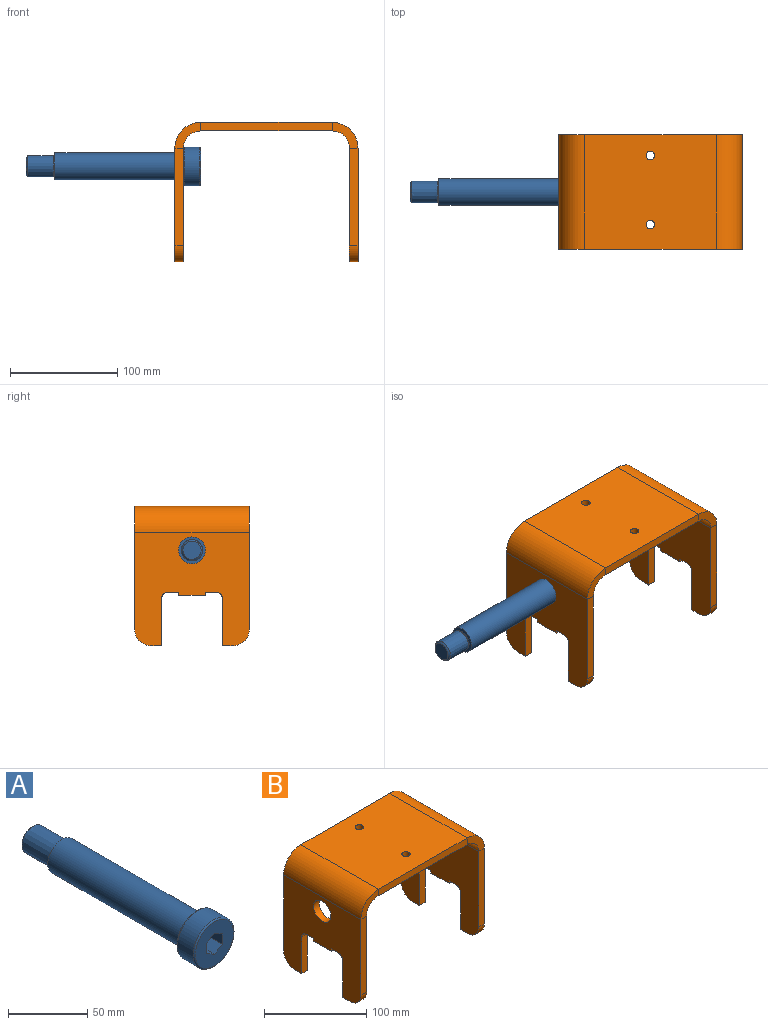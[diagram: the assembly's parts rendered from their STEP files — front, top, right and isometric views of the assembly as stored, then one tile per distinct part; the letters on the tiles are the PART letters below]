
ASSEMBLY  parts=2 mates=1
PART A: 20 faces, bbox 39x163x39 mm
  f0: plane 25x25mm, normal (0,1,0), area 222.1mm2, adj f14,f16
  f1: cylinder r=18mm len=36mm, axis (0,-1,0), area 1583.4mm2, adj f11,f12
  f2: plane 34x34mm, normal (0,1,0), area 492.4mm2, adj f12,f13
  f3: plane 34x34mm, normal (0,-1,0), area 738.2mm2, adj f4,f5,f6,f7,f8,f9,f11
  f4: plane 11x8.08mm, normal (-1,0,0), area 88.9mm2, adj f3,f5,f9,f10
  f5: plane 11x7.01mm, normal (-0.5,0,-0.87), area 88.9mm2, adj f3,f4,f6,f10
  f6: plane 11x6.99mm, normal (0.5,0,-0.86), area 88.9mm2, adj f3,f5,f7,f10
  f7: plane 11x8.08mm, normal (1,0,0), area 88.9mm2, adj f3,f6,f8,f10
  f8: plane 11x7.01mm, normal (0.5,0,0.87), area 88.9mm2, adj f3,f7,f9,f10
  f9: plane 11x6.99mm, normal (-0.5,0,0.86), area 88.9mm2, adj f3,f4,f8,f10
  f10: plane 16.17x14.02mm, normal (0,-1,0), area 169.7mm2, adj f4,f5,f6,f7,f8,f9
  f11: torus R=17mm, axis (0,-1,0), area 174.1mm2, adj f1,f3
  f12: torus R=17mm, axis (0,-1,0), area 174.1mm2, adj f1,f2
  f13: cylinder r=11.5mm len=23mm, axis (0,-1,0), area 108.4mm2, adj f2,f15
  f14: cylinder r=12.5mm len=118.5mm, axis (0,-1,0), area 9307mm2, adj f0,f15
  f15: plane 25x25mm, normal (0,-1,0), area 75.4mm2, adj f13,f14
  f16: bspline ~20x20mm, area 103.4mm2, adj f0,f17
  f17: extruded ~24x20mm, area 1508mm2, adj f16,f19
  f18: plane 17.03x17.02mm, normal (0,1,0), area 227mm2, adj f19
  f19: bspline ~20x20mm, area 123.3mm2, adj f17,f18
PART B: 50 faces, bbox 171x107x130 mm
  f0: plane 123x8mm, normal (0,1,0), area 984mm2, adj f4,f5,f25,f46
  f1: plane 123x8mm, normal (0,-1,0), area 984mm2, adj f4,f5,f24,f47
  f2: cylinder r=4mm len=8mm, axis (0,0,1), area 201.1mm2, adj f4,f5
  f3: cylinder r=4mm len=8mm, axis (0,0,1), area 201.1mm2, adj f4,f5
  f4: plane 123x107mm, normal (0,0,-1), area 13060.5mm2, adj f0,f1,f2,f3,f27,f49
  f5: plane 123x107mm, normal (0,0,1), area 13060.5mm2, adj f0,f1,f2,f3,f26,f48
  f6: plane 9.9x8mm, normal (0,0,-1), area 79.2mm2, adj f7,f18,f19,f20
  f7: plane 8x3mm, normal (0,-1,0), area 24mm2, adj f6,f8,f18,f19
  f8: plane 25x8mm, normal (0,0,-1), area 200mm2, adj f7,f9,f18,f19
  f9: plane 8x3mm, normal (0,1,0), area 24mm2, adj f8,f10,f18,f19
  f10: plane 9.9x8mm, normal (0,0,-1), area 79.2mm2, adj f9,f18,f19,f21
  f11: plane 44x8mm, normal (0,-1,0), area 352mm2, adj f12,f18,f19,f21
  f12: plane 10.1x8mm, normal (0,0,-1), area 80.8mm2, adj f11,f18,f19,f22
  f13: plane 91x8mm, normal (0,1,0), area 728mm2, adj f18,f19,f22,f25
  f14: plane 91x8mm, normal (0,-1,0), area 728mm2, adj f18,f19,f23,f24
  f15: plane 10.1x8mm, normal (0,0,-1), area 80.8mm2, adj f17,f18,f19,f23
  f16: cylinder r=12mm len=24mm, axis (1,0,0), area 603.2mm2, adj f18,f19
  f17: plane 44x8mm, normal (0,1,0), area 352mm2, adj f15,f18,f19,f20
  f18: plane 107x106mm, normal (1,0,0), area 8043.5mm2, adj f6,f7,f8,f9,f10,f11,f12,f13
  f19: plane 107x106mm, normal (-1,0,0), area 8043.5mm2, adj f6,f7,f8,f9,f10,f11,f12,f13
  f20: cylinder r=6mm len=8mm, axis (-1,0,0), area 75.4mm2, adj f6,f17,f18,f19
  f21: cylinder r=6mm len=8mm, axis (-1,0,0), area 75.4mm2, adj f10,f11,f18,f19
  f22: cylinder r=15mm len=15mm, axis (1,0,0), area 188.5mm2, adj f12,f13,f18,f19
  f23: cylinder r=15mm len=15mm, axis (1,0,0), area 188.5mm2, adj f14,f15,f18,f19
  f24: plane 24x24mm, normal (0,-1,0), area 251.3mm2, adj f1,f14,f26,f27
  f25: plane 24x24mm, normal (0,1,0), area 251.3mm2, adj f0,f13,f26,f27
  f26: cylinder r=24mm len=107mm, axis (0,-1,0), area 4033.8mm2, adj f5,f19,f24,f25
  f27: cylinder r=16mm len=107mm, axis (0,-1,0), area 2689.2mm2, adj f4,f18,f24,f25
  f28: plane 9.9x8mm, normal (0,0,-1), area 79.2mm2, adj f29,f40,f41,f45
  f29: plane 8x3mm, normal (0,1,0), area 24mm2, adj f28,f30,f40,f41
  f30: plane 25x8mm, normal (0,0,-1), area 200mm2, adj f29,f31,f40,f41
  f31: plane 8x3mm, normal (0,-1,0), area 24mm2, adj f30,f32,f40,f41
  f32: plane 9.9x8mm, normal (0,0,-1), area 79.2mm2, adj f31,f40,f41,f44
  f33: plane 44x8mm, normal (0,1,0), area 352mm2, adj f34,f40,f41,f44
  f34: plane 10.1x8mm, normal (0,0,-1), area 80.8mm2, adj f33,f40,f41,f43
  f35: plane 91x8mm, normal (0,-1,0), area 728mm2, adj f40,f41,f43,f47
  f36: plane 91x8mm, normal (0,1,0), area 728mm2, adj f40,f41,f42,f46
  f37: plane 10.1x8mm, normal (0,0,-1), area 80.8mm2, adj f39,f40,f41,f42
  f38: cylinder r=12mm len=24mm, axis (-1,0,0), area 603.2mm2, adj f40,f41
  f39: plane 44x8mm, normal (0,-1,0), area 352mm2, adj f37,f40,f41,f45
  f40: plane 107x106mm, normal (-1,0,0), area 8043.5mm2, adj f28,f29,f30,f31,f32,f33,f34,f35
  f41: plane 107x106mm, normal (1,0,0), area 8043.5mm2, adj f28,f29,f30,f31,f32,f33,f34,f35
  f42: cylinder r=15mm len=15mm, axis (-1,0,0), area 188.5mm2, adj f36,f37,f40,f41
  f43: cylinder r=15mm len=15mm, axis (-1,0,0), area 188.5mm2, adj f34,f35,f40,f41
  f44: cylinder r=6mm len=8mm, axis (1,0,0), area 75.4mm2, adj f32,f33,f40,f41
  f45: cylinder r=6mm len=8mm, axis (1,0,0), area 75.4mm2, adj f28,f39,f40,f41
  f46: plane 24x24mm, normal (0,1,0), area 251.3mm2, adj f0,f36,f48,f49
  f47: plane 24x24mm, normal (0,-1,0), area 251.3mm2, adj f1,f35,f48,f49
  f48: cylinder r=24mm len=107mm, axis (0,1,0), area 4033.8mm2, adj f5,f41,f46,f47
  f49: cylinder r=16mm len=107mm, axis (0,1,0), area 2689.2mm2, adj f4,f40,f46,f47
PLACE A rot(axis=(0,0,1),90deg) t=(12,53.5,-33)mm
PLACE B at identity
MATE fastened A.f13 <-> B.f16  axis (-1,0,0) through (-4,53.5,-33)mm
